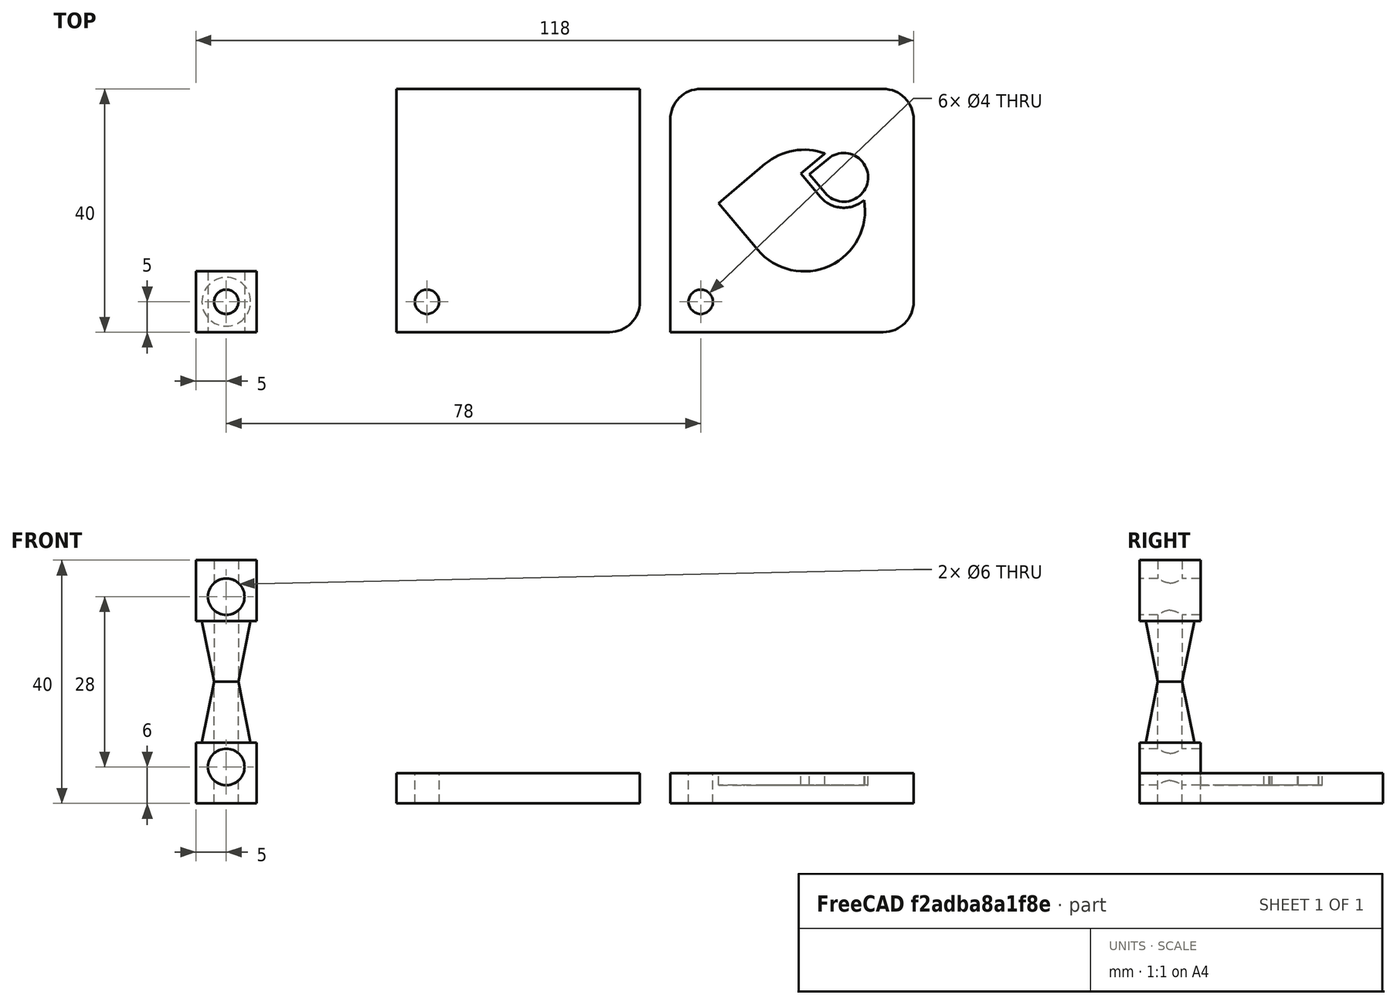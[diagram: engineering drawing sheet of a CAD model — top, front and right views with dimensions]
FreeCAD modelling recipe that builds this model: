
FCSTD DOCUMENT  (FreeCAD 0.16R6710 (Git))
Label: Test1
License: All rights reserved
LicenseURL: http://en.wikipedia.org/wiki/All_rights_reserved
objects: Part::Cylinder×9, Part::Cut×8, Part::Box×7, Part::Fuse×6, Part::Fillet×4, Part::Cone×2, Part::Mirroring×1, Part::MultiFuse×1, Part::FeaturePython×1
note: 39 computed .brp shape members not serialized (recipe doc carries the construction recipe); baked Part::Feature solids carry a one-line shape summary decoded from their .brp

FEATURE [Part::Box] Box  label="Cube"
  Height = 10
  Length = 10
  Width = 10
FEATURE [Part::Cylinder] Cylinder
  Angle = 360
  Height = 100
  Placement = pos=(5,10,6) rot=(1,0,0;1.5708rad)
  Radius = 3
FEATURE [Part::Cut] Cut
  Base = -> Box
  Tool = -> Cylinder
FEATURE [Part::Cone] Cone
  Angle = 360
  Height = 10
  Placement = pos=(5,5,10) rot=(0,0,1;0rad)
  Radius1 = 4
  Radius2 = 2
FEATURE [Part::Fuse] Fusion
  Base = -> Cut
  Tool = -> Cone
FEATURE [Part::Cylinder] Cylinder001
  Angle = 360
  Height = 22
  Placement = pos=(5,5,-1) rot=(0,0,1;0rad)
  Radius = 2
FEATURE [Part::Cut] Cut001
  Base = -> Fusion
  Tool = -> Cylinder001
FEATURE [Part::Box] Box001  label="Cube001"
  Height = 10
  Length = 10
  Width = 10
FEATURE [Part::Cylinder] Cylinder002
  Angle = 360
  Height = 100
  Placement = pos=(5,10,6) rot=(1,0,0;1.5708rad)
  Radius = 3
FEATURE [Part::Cut] Cut002
  Base = -> Box001
  Tool = -> Cylinder002
FEATURE [Part::Cone] Cone001
  Angle = 360
  Height = 10
  Placement = pos=(5,5,10) rot=(0,0,1;0rad)
  Radius1 = 4
  Radius2 = 2
FEATURE [Part::Fuse] Fusion001
  Base = -> Cut002
  Tool = -> Cone001
FEATURE [Part::Cylinder] Cylinder003
  Angle = 360
  Height = 22
  Placement = pos=(5,5,-1) rot=(0,0,1;0rad)
  Radius = 2
FEATURE [Part::Cut] Cut003
  Base = -> Fusion001
  Placement = pos=(23,0,0) rot=(0,0,1;0rad)
  Tool = -> Cylinder003
FEATURE [Part::Mirroring] Part__Mirroring  label="Cut003 (Mirror #1)"
  Base = (0,0,0)
  Normal = (0,0,1)
  Placement = pos=(-23,0,40) rot=(0,0,1;0rad)
  Source = -> Cut003
FEATURE [Part::Fuse] Fusion002
  Base = -> Cut001
  Placement = pos=(-33,0,0) rot=(0,0,1;0rad)
  Tool = -> Part__Mirroring
FEATURE [Part::Box] Box002  label="Cube002"
  Height = 5
  Length = 40
  Width = 40
FEATURE [Part::Cylinder] Cylinder004
  Angle = 360
  Height = 10
  Placement = pos=(5,5,0) rot=(0,0,1;0rad)
  Radius = 2
FEATURE [Part::Cut] Cut004
  Base = -> Box002
  Tool = -> Cylinder004
FEATURE [Part::Fillet] Fillet
  Base = -> Cut004
  Edges = 1 edges r=5: [Edge6]
FEATURE [Part::Fillet] Fillet001
  Base = -> Fillet
  Edges = 1 edges r=5: [Edge17]
FEATURE [Part::Fillet] Fillet002
  Base = -> Fillet001
  Edges = 1 edges r=5: [Edge15]
  Placement = pos=(45,0,0) rot=(0,0,1;0rad)
FEATURE [Part::Box] Box004  label="Cube004"
  Height = 5
  Length = 40
  Width = 40
FEATURE [Part::Cylinder] Cylinder005
  Angle = 360
  Height = 10
  Placement = pos=(5,5,0) rot=(0,0,1;0rad)
  Radius = 2
FEATURE [Part::Cut] Cut006
  Base = -> Box004
  Tool = -> Cylinder005
FEATURE [Part::Fillet] Fillet003
  Base = -> Cut006
  Edges = 1 edges r=5: [Edge6]
FEATURE [Part::Cylinder] Cylinder006
  Angle = 360
  Height = 10
  Radius = 20
FEATURE [Part::Box] Box005  label="Cube005"
  Height = 10
  Length = 20
  Placement = pos=(0,-20,0) rot=(0,0,1;0rad)
  Width = 20
FEATURE [Part::Fuse] Fusion003
  Base = -> Cylinder006
  Tool = -> Box005
FEATURE [Part::Cylinder] Cylinder007
  Angle = 360
  Height = 12
  Placement = pos=(0,0,-1) rot=(0,0,1;0rad)
  Radius = 10
FEATURE [Part::Box] Box006  label="Cube006"
  Height = 12
  Length = 10
  Placement = pos=(0,-10,-1) rot=(0,0,1;0rad)
  Width = 10
FEATURE [Part::Fuse] Fusion004
  Base = -> Cylinder007
  Placement = pos=(-17,0,0) rot=(0,0,1;0rad)
  Tool = -> Box006
FEATURE [Part::Cylinder] Cylinder008
  Angle = 360
  Height = 10
  Radius = 8
FEATURE [Part::Box] Box003  label="Cube003"
  Height = 10
  Length = 8
  Placement = pos=(0,-8,0) rot=(0,0,1;0rad)
  Width = 8
FEATURE [Part::MultiFuse] Fusion005
  Placement = pos=(-17,0,0) rot=(0,0,1;0rad)
  Shapes = -> [Cylinder008,Box003]
FEATURE [Part::Cut] Cut007
  Base = -> Fusion003
  Tool = -> Fusion004
FEATURE [Part::Fuse] Fusion006  label="rrl-logo"
  Base = -> Fusion005
  Placement = pos=(0,0,0) rot=(0,0,1;3.83972rad)
  Tool = -> Cut007
FEATURE [Part::FeaturePython] Clone  label="Clone of rrl-logo"  # Draft clone (typed FeaturePython)
  Objects = -> [Fusion006]
  Placement = pos=(67,20,3) rot=(0,0,1;3.83972rad)
  Scale = (0.5,0.5,0.5)
FEATURE [Part::Cut] Cut008
  Base = -> Fillet002
  Tool = -> Clone
